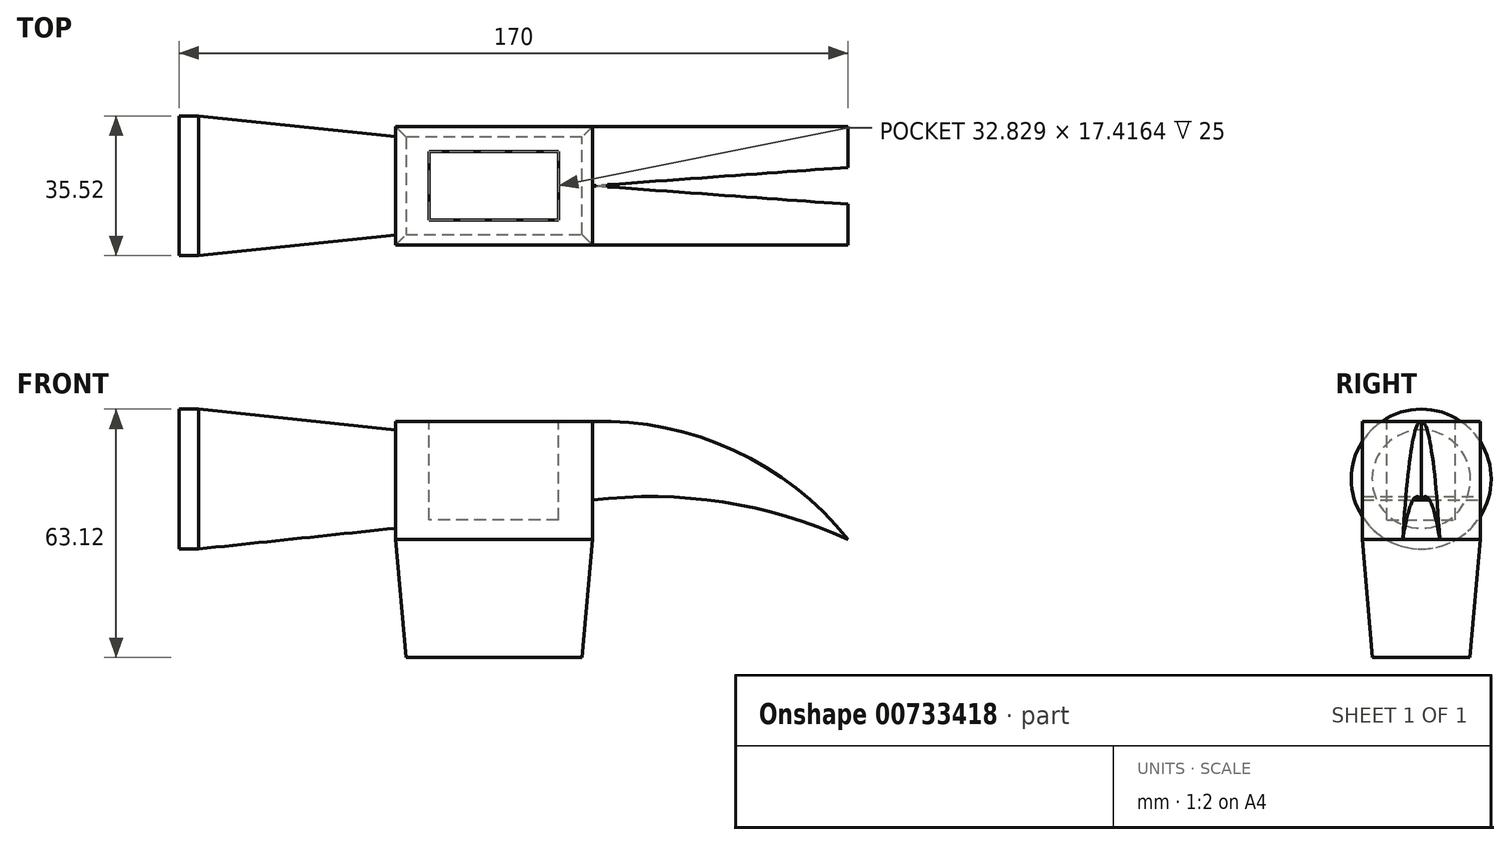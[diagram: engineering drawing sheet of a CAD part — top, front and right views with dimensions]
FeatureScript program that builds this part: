
annotation { "Feature Type Name" : "Feature", "Feature Type Description" : "" }
export const myFeature = defineFeature(function(context is Context, id is Id, definition is map)
    precondition{}
    {
        {
            var Q0;
            Q0=qCreatedBy(makeId("Front.planeOp"),FACE);
            var sketch = newSketch(context, id + "F0", { "sketchPlane" : qUnion([Q0])});
            skLineSegment(sketch, "E0.bottom", {"start": v(0, 0) * mm, "end": v(50, 0) * mm});
            skLineSegment(sketch, "E0.top", {"start": v(0, 30) * mm, "end": v(50, 30) * mm});
            skLineSegment(sketch, "E0.left", {"start": v(0, 0) * mm, "end": v(0, 30) * mm});
            skLineSegment(sketch, "E0.right", {"start": v(50, 0) * mm, "end": v(50, 30) * mm});
            skSolve(sketch);
        }
        {
            var Q0;
            Q0=makeQuery(id+"F0.imprint","IMPRINT",FACE,{"disambiguationData":[TD([[makeQuery(id+"F0.imprint","IMPRINT",EDGE,{"derivedFrom":sQuery(id+"F0.wireOp",EDGE,"E0.bottom")}),1.0]])]});
            extrude(context, id + "F1", {"entities" : qUnion([Q0]), "endBound" : BoundingType.SYMMETRIC, "depth" : 30 * mm, "offsetDistance" : 25 * mm});
        }
        {
            var Q0;
            Q0=makeQuery(id+"F1.opExtrude","SWEPT_FACE",FACE,{"disambiguationData":[OSD([sQuery(id+"F0.wireOp",EDGE,"E0.bottom")])]});
            extrude(context, id + "F2", {"entities" : qUnion([Q0]), "operationType" : NewBodyOperationType.ADD, "depth" : 30 * mm, "offsetDistance" : 25 * mm, "hasDraft" : true, "draftAngle" : 5 * degree, "draftPullDirection" : true});
        }
        {
            var Q0;
            Q0=qCreatedBy(makeId("Right.planeOp"),FACE);
            var sketch = newSketch(context, id + "F3", { "sketchPlane" : qUnion([Q0])});
            skCircle(sketch, "E1", {"center": v(0, 15.37) * mm, "radius": 12.5 * mm});
            skSolve(sketch);
        }
        {
            var Q0;
            Q0=makeQuery(id+"F3.imprint","IMPRINT",FACE,{"disambiguationData":[TD([[makeQuery(id+"F3.imprint","IMPRINT",EDGE,{"derivedFrom":sQuery(id+"F3.wireOp",EDGE,"E1")}),1.0]])]});
            extrude(context, id + "F4", {"entities" : qUnion([Q0]), "operationType" : NewBodyOperationType.ADD, "oppositeDirection" : true, "depth" : 50 * mm, "offsetDistance" : 25 * mm, "hasDraft" : true, "draftAngle" : 6 * degree});
        }
        {
            var Q0;
            Q0=qCreatedBy(makeId("Front.planeOp"),FACE);
            var sketch = newSketch(context, id + "F5", { "sketchPlane" : qUnion([Q0])});
            skLineSegment(sketch, "E2.0", {"start": v(115, 0) * mm, "end": v(115, 65.84) * mm});
            skArc(sketch, "E3", {"start": v(115, 0) * mm, "mid": v(86.03, 22.63) * mm, "end": v(50, 29.98) * mm});
            skArc(sketch, "E4", {"start": v(115, 0) * mm, "mid": v(83.2, 9.52) * mm, "end": v(50, 10) * mm});
            skLineSegment(sketch, "E5", {"start": v(50, 10) * mm, "end": v(50, 29.98) * mm});
            skSolve(sketch);
        }
        {
            var Q0;
            Q0=makeQuery(id+"F5.imprint","IMPRINT",FACE,{"disambiguationData":[TD([[makeQuery(id+"F5.imprint","IMPRINT",EDGE,{"derivedFrom":sQuery(id+"F5.wireOp",EDGE,"E3")}),1.0]])]});
            extrude(context, id + "F6", {"entities" : qUnion([Q0]), "endBound" : BoundingType.SYMMETRIC, "depth" : 30 * mm, "offsetDistance" : 25 * mm});
        }
        {
            var Q0;
            Q0=makeQuery(id+"F4.opExtrude","CAP_FACE",FACE,{"disambiguationData":[OSD([sQuery(id+"F3.wireOp",EDGE,"E1")])],"isStart":false});
            extrude(context, id + "F7", {"entities" : qUnion([Q0]), "operationType" : NewBodyOperationType.ADD, "depth" : 5 * mm, "offsetDistance" : 25 * mm});
        }
        {
            var Q0;
            Q0=qCreatedBy(makeId("Top.planeOp"),FACE);
            var sketch = newSketch(context, id + "F8", { "sketchPlane" : qUnion([Q0])});
            skLineSegment(sketch, "E6", {"start": v(50.04, 5) * mm, "end": v(50.04, -5) * mm});
            skLineSegment(sketch, "E7", {"start": v(50.04, 0) * mm, "end": v(119.24, 5) * mm});
            skLineSegment(sketch, "E8", {"start": v(50.04, 0) * mm, "end": v(119.24, -5) * mm});
            skLineSegment(sketch, "E9", {"start": v(119.24, 5) * mm, "end": v(119.24, -5) * mm});
            skSolve(sketch);
        }
        {
            var Q0;
            Q0 = qSketchRegion(id + "F8", true);
            extrude(context, id + "F9", {"entities" : qUnion([Q0]), "operationType" : NewBodyOperationType.REMOVE, "endBound" : BoundingType.SYMMETRIC, "oppositeDirection" : true, "depth" : 60 * mm, "offsetDistance" : 25 * mm});
        }
        {
            var Q0;
            Q0=makeQuery(id+"F1.opExtrude","SWEPT_FACE",FACE,{"disambiguationData":[OSD([sQuery(id+"F0.wireOp",EDGE,"E0.top")])]});
            var sketch = newSketch(context, id + "F10", { "sketchPlane" : qUnion([Q0])});
            skLineSegment(sketch, "E10.bottom", {"start": v(41.41, -8.7) * mm, "end": v(8.59, -8.7) * mm});
            skLineSegment(sketch, "E10.top", {"start": v(41.41, 8.7) * mm, "end": v(8.59, 8.7) * mm});
            skLineSegment(sketch, "E10.left", {"start": v(41.41, -8.7) * mm, "end": v(41.41, 8.7) * mm});
            skLineSegment(sketch, "E10.right", {"start": v(8.59, -8.7) * mm, "end": v(8.59, 8.7) * mm});
            skPoint(sketch, "E10.middle", {"position": v(25, 0) * mm});
            skSolve(sketch);
        }
        {
            var Q0;
            Q0=makeQuery(id+"F10.imprint","IMPRINT",FACE,{"disambiguationData":[TD([[makeQuery(id+"F10.imprint","IMPRINT",EDGE,{"derivedFrom":sQuery(id+"F10.wireOp",EDGE,"E10.bottom")}),-1.0]])]});
            extrude(context, id + "F11", {"entities" : qUnion([Q0]), "operationType" : NewBodyOperationType.REMOVE, "oppositeDirection" : true, "depth" : 25 * mm, "offsetDistance" : 25 * mm});
        }
    });
